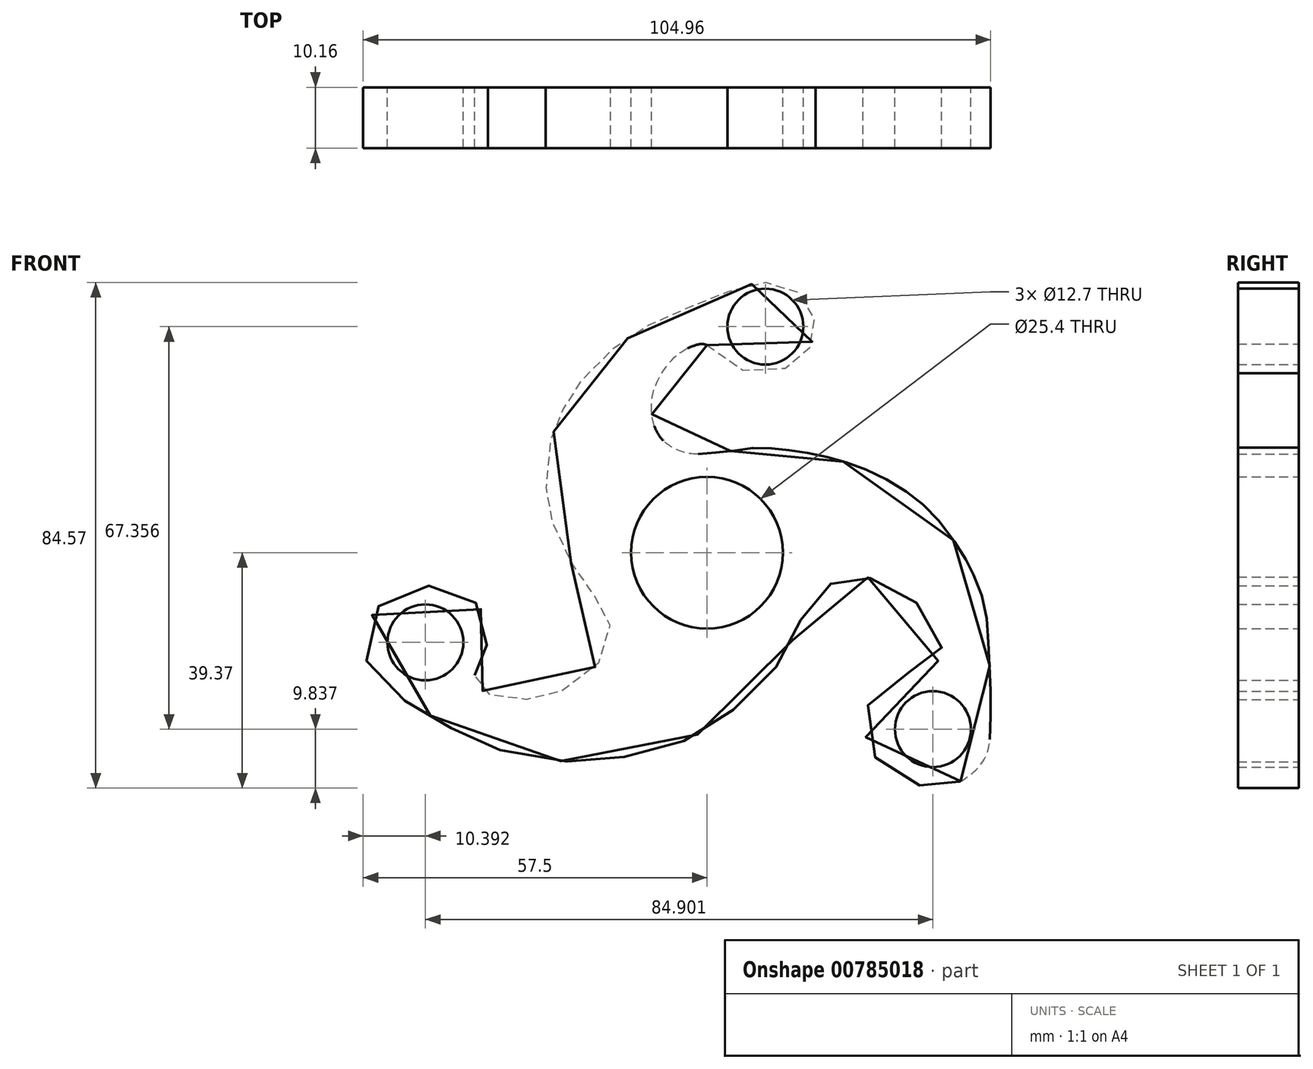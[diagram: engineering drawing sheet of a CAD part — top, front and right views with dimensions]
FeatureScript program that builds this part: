
annotation { "Feature Type Name" : "Feature", "Feature Type Description" : "" }
export const myFeature = defineFeature(function(context is Context, id is Id, definition is map)
    precondition{}
    {
        {
            var Q0;
            Q0=qCreatedBy(makeId("Front.planeOp"),FACE);
            var sketch = newSketch(context, id + "F0", { "sketchPlane" : qUnion([Q0])});
            skFitSpline(sketch, "E0", {"points": [v(0, 34.73) * mm, v(4.83, 31.12) * mm, v(10.44, 30.12) * mm, v(15.37, 32.03) * mm, v(17.04, 34) * mm, v(18.11, 37.27) * mm, v(18, 39.12) * mm, v(16.95, 42.1) * mm, v(14.3, 44.02) * mm, v(10.65, 45.16) * mm, v(6.03, 44.56) * mm, v(1.1, 42.64) * mm, v(-4.11, 40.6) * mm, v(-9.81, 38.02) * mm, v(-14.74, 34.84) * mm, v(-19.12, 31.06) * mm, v(-22.72, 26.38) * mm, v(-24.01, 24.2) * mm, v(-25.37, 21.04) * mm, v(-26.55, 16.88) * mm, v(-26.98, 9.92) * mm, v(-26.85, 8.09) * mm, v(-23.73, 0) * mm, v(-21.63, -3.23) * mm, v(-18.75, -7.4) * mm, v(-16.98, -9.91) * mm, v(-16.17, -14.05) * mm, v(-18.6, -19) * mm, v(-24.03, -23.04) * mm, v(-27.89, -24.26) * mm, v(-32.6, -24.58) * mm, v(-36.42, -23.76) * mm, v(-38.2, -22.44) * mm, v(-38.84, -20.47) * mm, v(-38.38, -18.94) * mm, v(-37.34, -17.16) * mm, v(-36.8, -15.36) * mm, v(-36.73, -12.24) * mm, v(-38.3, -8.82) * mm, v(-41.71, -6.36) * mm, v(-46.4, -5.52) * mm, v(-51.55, -6.6) * mm, v(-55.63, -9.84) * mm, v(-57.5, -15.96) * mm, v(-55.75, -20.1) * mm, v(-51.65, -24.01) * mm, v(-47.16, -26.7) * mm, v(-43.06, -29.23) * mm, v(-37.78, -31.63) * mm, v(-34.06, -33.2) * mm, v(-25.54, -34.8) * mm, v(-19.93, -34.89) * mm, v(-13.9, -34.2) * mm, v(-7.71, -32.85) * mm, v(-1.52, -30.39) * mm, v(3.06, -27.25) * mm, v(8.25, -23.08) * mm, v(12.03, -18.46) * mm, v(14.37, -14.56) * mm, v(16.35, -9.76) * mm, v(19.05, -6.34) * mm, v(21.2, -4.96) * mm, v(23.87, -4.32) * mm, v(26.65, -4.1) * mm, v(30.86, -5.68) * mm, v(35, -8.32) * mm, v(38.14, -12.46) * mm, v(39.25, -16.25) * mm, v(37.79, -18.97) * mm, v(34.05, -19.93) * mm, v(29.76, -21.65) * mm, v(26.64, -26.19) * mm, v(26.28, -29.87) * mm, v(29.58, -36.16) * mm, v(33.49, -38.37) * mm, v(37.52, -39.3) * mm, v(40.23, -39.17) * mm, v(42.65, -38.11) * mm, v(44.99, -36.33) * mm, v(46.85, -33.57) * mm, v(47.46, -28.32) * mm, v(47.36, -20.95) * mm, v(47.05, -14.5) * mm, v(46.25, -8.13) * mm, v(44.23, -2.99) * mm, v(42.61, 0) * mm, v(38.43, 5.78) * mm, v(34.4, 9.44) * mm, v(29.43, 12.56) * mm, v(24.26, 14.78) * mm, v(19.94, 16.04) * mm, v(15.38, 16.94) * mm, v(11.9, 17.36) * mm, v(7.88, 17.54) * mm, v(4.12, 17.01) * mm, v(0, 16.62) * mm, v(-3.05, 16.62) * mm, v(-6.02, 17.76) * mm, v(-7.87, 19.4) * mm, v(-8.98, 21.8) * mm, v(-9.3, 24.61) * mm, v(-8.76, 27.54) * mm, v(-7.03, 30.8) * mm, v(-4.63, 33.39) * mm, v(-1.93, 34.7) * mm, v(0, 34.73) * mm]});
            skCircle(sketch, "E1", {"center": v(9.76, 37.82) * mm, "radius": 6.35 * mm});
            skCircle(sketch, "E2", {"center": v(37.8, -29.53) * mm, "radius": 6.35 * mm});
            skCircle(sketch, "E3", {"center": v(-47.1, -15.01) * mm, "radius": 6.35 * mm});
            skCircle(sketch, "E4", {"center": v(0, 0) * mm, "radius": 12.7 * mm});
            skSolve(sketch);
        }
        {
            var Q0;
            Q0 = qSketchRegion(id + "F0", true);
            extrude(context, id + "F1", {"entities" : qUnion([Q0]), "depth" : 10.16 * mm, "offsetDistance" : 25.4 * mm});
        }
    });
